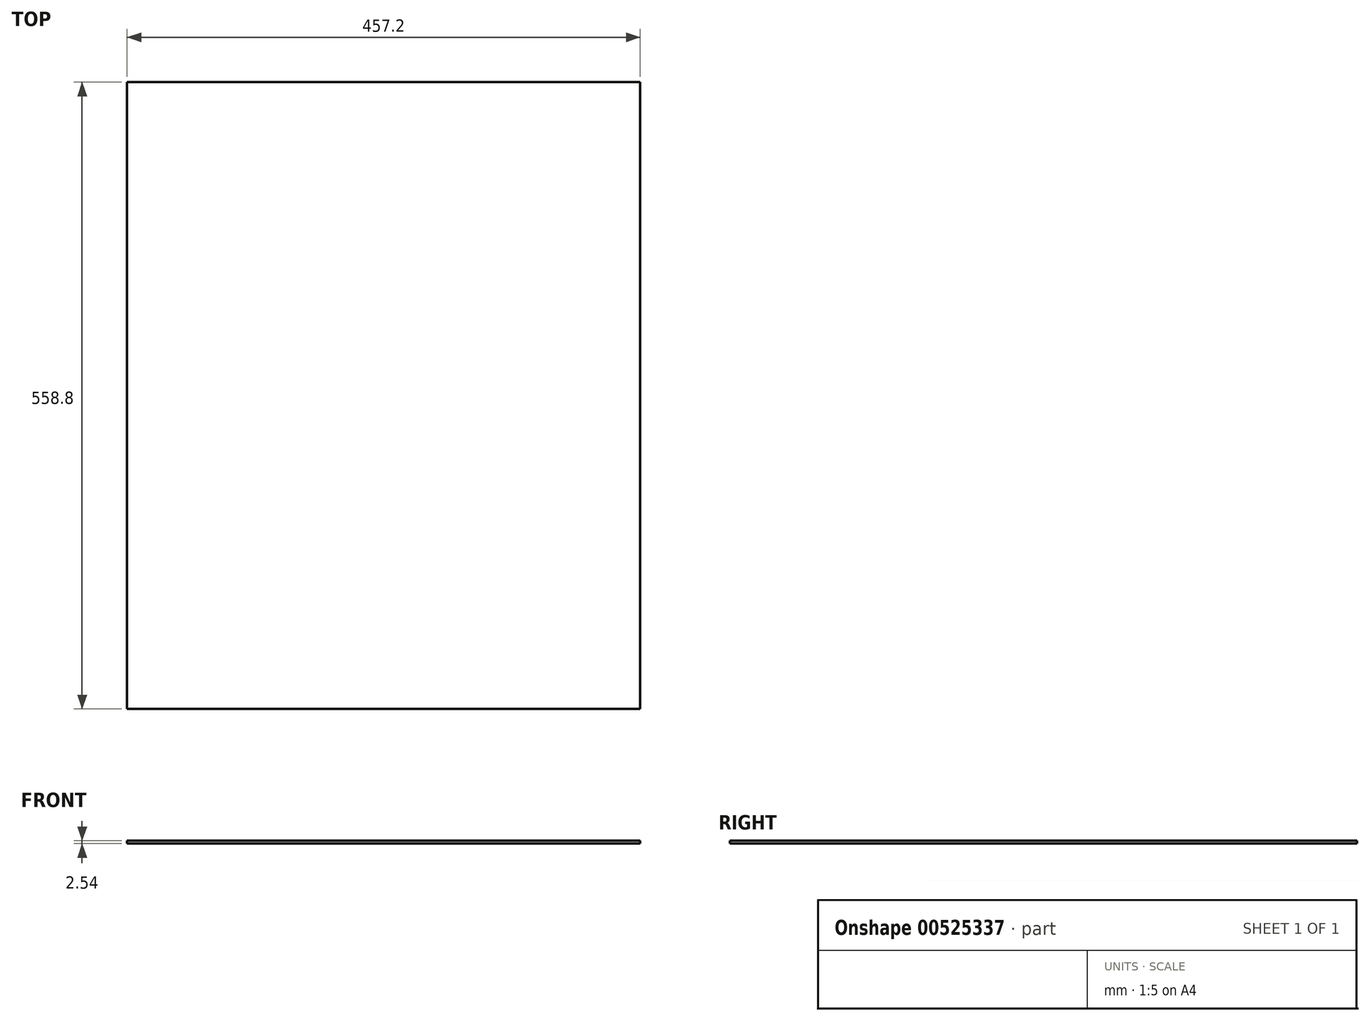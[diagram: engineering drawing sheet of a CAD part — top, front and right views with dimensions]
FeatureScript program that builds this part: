
annotation { "Feature Type Name" : "Feature", "Feature Type Description" : "" }
export const myFeature = defineFeature(function(context is Context, id is Id, definition is map)
    precondition{}
    {
        {
            var Q0;
            Q0=qCreatedBy(makeId("Top.planeOp"),FACE);
            var sketch = newSketch(context, id + "F0", { "sketchPlane" : qUnion([Q0])});
            skLineSegment(sketch, "E0.bottom", {"start": v(228.6, 50.8) * mm, "end": v(-228.6, 50.8) * mm});
            skLineSegment(sketch, "E0.top", {"start": v(228.6, -50.8) * mm, "end": v(-228.6, -50.8) * mm});
            skLineSegment(sketch, "E0.left", {"start": v(228.6, 50.8) * mm, "end": v(228.6, -50.8) * mm});
            skLineSegment(sketch, "E0.right", {"start": v(-228.6, 50.8) * mm, "end": v(-228.6, -50.8) * mm});
            skPoint(sketch, "E0.middle", {"position": v(0, 0) * mm});
            skSolve(sketch);
        }
        {
            var Q0;
            Q0=makeQuery(id+"F0.imprint","IMPRINT",FACE,{"disambiguationData":[TD([[makeQuery(id+"F0.imprint","IMPRINT",EDGE,{"derivedFrom":sQuery(id+"F0.wireOp",EDGE,"E0.bottom")}),1.0]])]});
            extrude(context, id + "F1", {"entities" : qUnion([Q0]), "depth" : 2.54 * mm, "offsetDistance" : 25.4 * mm});
        }
        {
            var Q0;
            Q0=makeQuery(id+"F1.opExtrude","SWEPT_FACE",FACE,{"disambiguationData":[OSD([sQuery(id+"F0.wireOp",EDGE,"E0.bottom")])]});
            var sketch = newSketch(context, id + "F2", { "sketchPlane" : qUnion([Q0])});
            skLineSegment(sketch, "E1.bottom", {"start": v(-228.6, 2.54) * mm, "end": v(228.6, 2.54) * mm});
            skLineSegment(sketch, "E1.top", {"start": v(-228.6, 0) * mm, "end": v(228.6, 0) * mm});
            skLineSegment(sketch, "E1.left", {"start": v(-228.6, 2.54) * mm, "end": v(-228.6, 0) * mm});
            skLineSegment(sketch, "E1.right", {"start": v(228.6, 2.54) * mm, "end": v(228.6, 0) * mm});
            skSolve(sketch);
        }
        {
            var Q0;
            Q0 = qSketchRegion(id + "F2", true);
            extrude(context, id + "F3", {"entities" : qUnion([Q0]), "operationType" : NewBodyOperationType.ADD, "depth" : 457.2 * mm, "offsetDistance" : 25.4 * mm});
        }
    });
